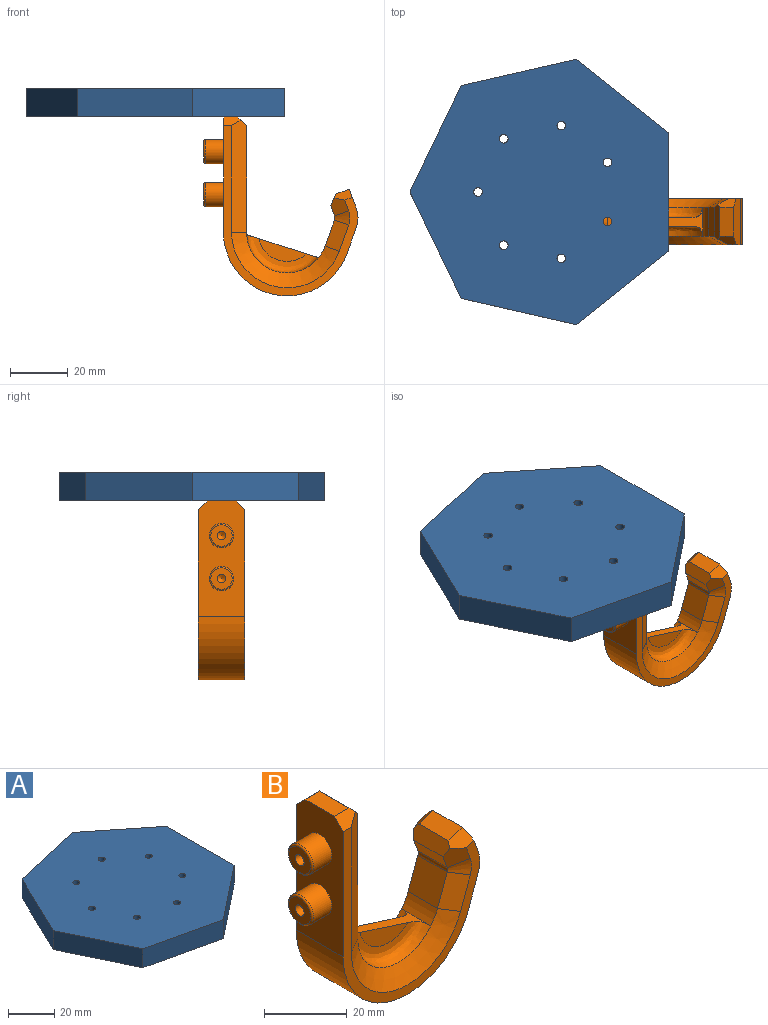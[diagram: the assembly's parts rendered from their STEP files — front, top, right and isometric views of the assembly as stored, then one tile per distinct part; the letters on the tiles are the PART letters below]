
ASSEMBLY  parts=2 mates=1
PART A: 16 faces, bbox 89.7x92x10 mm
  f0: plane 40.93x10mm, normal (1,0,0), area 409.3mm2, adj f1,f6,f7,f8
  f1: plane 32x25.52mm, normal (0.62,0.78,0), area 409.3mm2, adj f0,f2,f7,f8
  f2: plane 39.91x10mm, normal (-0.22,0.97,0), area 409.3mm2, adj f1,f3,f7,f8
  f3: plane 36.88x17.76mm, normal (-0.9,0.43,0), area 409.3mm2, adj f2,f4,f7,f8
  f4: plane 36.88x17.76mm, normal (-0.9,-0.43,0), area 409.3mm2, adj f3,f5,f7,f8
  f5: plane 39.91x10mm, normal (-0.22,-0.97,0), area 409.3mm2, adj f4,f6,f7,f8
  f6: plane 32x25.52mm, normal (0.62,-0.78,0), area 409.3mm2, adj f0,f5,f7,f8
  f7: plane 91.98x89.67mm, normal (0,0,1), area 6039.4mm2, adj f0,f1,f2,f3,f4,f5,f6,f9
  f8: plane 91.98x89.67mm, normal (0,0,-1), area 6039.4mm2, adj f0,f1,f2,f3,f4,f5,f6,f9
  f9: cylinder r=1.5mm len=10mm, axis (0,0,-1), area 94.2mm2, adj f7,f8
  f10: cylinder r=1.5mm len=10mm, axis (0,0,-1), area 94.2mm2, adj f7,f8
  f11: cylinder r=1.5mm len=10mm, axis (0,0,-1), area 94.2mm2, adj f7,f8
  f12: cylinder r=1.5mm len=10mm, axis (0,0,-1), area 94.2mm2, adj f7,f8
  f13: cylinder r=1.5mm len=10mm, axis (0,0,-1), area 94.2mm2, adj f7,f8
  f14: cylinder r=1.5mm len=10mm, axis (0,0,-1), area 94.2mm2, adj f7,f8
  f15: cylinder r=1.5mm len=10mm, axis (0,0,-1), area 94.2mm2, adj f7,f8
PART B: 46 faces, bbox 54.6x17.2x63.2 mm
  f0: cylinder r=14mm len=10mm, axis (0,-1,0), area 45.7mm2, adj f10,f12,f13,f35
  f1: plane 10x5mm, normal (0,0,1), area 50mm2, adj f6,f41,f42,f43
  f2: plane 10x4.7mm, normal (-0.34,0,0.94), area 50mm2, adj f23,f38,f39,f40
  f3: plane 37x10mm, normal (1,0,0), area 370mm2, adj f4,f8,f9,f43
  f4: plane 38.9x5.2mm, normal (0.5,-0.87,0), area 227.8mm2, adj f3,f5,f10,f42,f43
  f5: plane 59x46.59mm, normal (0,-1,0), area 319.8mm2, adj f4,f6,f10,f11,f14,f15,f18,f19
  f6: plane 40x16mm, normal (-1,0,0), area 520.2mm2, adj f1,f5,f7,f11,f25,f27,f41,f42
  f7: plane 59x46.59mm, normal (0,1,0), area 319.8mm2, adj f6,f8,f11,f12,f15,f16,f19,f20
  f8: plane 38.9x5.2mm, normal (0.5,0.87,0), area 227.8mm2, adj f3,f7,f12,f41,f43
  f9: cylinder r=14mm len=10mm, axis (0,-1,0), area 8.4mm2, adj f3,f10,f12,f35
  f10: cone r=14mm half-angle=60deg, axis (0,-1,0), area 278.3mm2, adj f0,f4,f5,f9,f14,f36
  f11: cylinder r=22mm len=42.67mm, axis (0,-1,0), area 983mm2, adj f5,f6,f7,f15
  f12: cone r=19.2mm half-angle=60deg, axis (0,1,0), area 278.3mm2, adj f0,f7,f8,f9,f16,f37
  f13: plane 10x9.1mm, normal (-0.94,0,0.34), area 96.9mm2, adj f0,f14,f16,f17
  f14: plane 10.88x8.2mm, normal (-0.47,-0.87,0.17), area 58.2mm2, adj f5,f10,f13,f18
  f15: plane 16x9.1mm, normal (0.94,0,-0.34), area 155mm2, adj f5,f7,f11,f19
  f16: plane 10.88x8.2mm, normal (-0.47,0.87,0.17), area 58.2mm2, adj f7,f12,f13,f20
  f17: cylinder r=2mm len=10mm, axis (0,-1,0), area 14mm2, adj f13,f18,f20,f21
  f18: cone r=2mm half-angle=60deg, axis (0,-1,0), area 19.3mm2, adj f5,f14,f17,f22
  f19: cylinder r=10mm len=16mm, axis (0,-1,0), area 111.7mm2, adj f5,f7,f15,f23
  f20: cone r=7.2mm half-angle=60deg, axis (0,1,0), area 19.3mm2, adj f7,f16,f17,f24
  f21: plane 10x3.76mm, normal (-0.94,0,-0.34), area 40mm2, adj f17,f22,f24,f40
  f22: plane 6.26x6.2mm, normal (-0.47,-0.87,-0.17), area 29.7mm2, adj f5,f18,f21,f39,f40
  f23: plane 16x6.58mm, normal (0.94,0,0.34), area 103mm2, adj f2,f5,f7,f19,f38,f39
  f24: plane 6.26x6.2mm, normal (-0.47,0.87,-0.17), area 29.7mm2, adj f7,f20,f21,f38,f40
  f25: cylinder r=4.2mm len=8.4mm, axis (1,0,0), area 166.3mm2, adj f6,f45
  f26: plane 7.4x7.4mm, normal (-1,0,0), area 35.9mm2, adj f30,f45
  f27: cylinder r=4.2mm len=8.4mm, axis (1,0,0), area 166.3mm2, adj f6,f44
  f28: plane 7.4x7.4mm, normal (-1,0,0), area 35.9mm2, adj f32,f44
  f29: cone r=0mm half-angle=59deg, axis (-1,0,0), area 8.2mm2, adj f30
  f30: cylinder r=1.5mm len=12mm, axis (-1,0,0), area 113.1mm2, adj f26,f29
  f31: cone r=0mm half-angle=59deg, axis (-1,0,0), area 8.2mm2, adj f32
  f32: cylinder r=1.5mm len=12mm, axis (-1,0,0), area 113.1mm2, adj f28,f31
  f33: plane 16.55x7.9mm, normal (0,-1,0), area 61.6mm2, adj f35,f36
  f34: plane 16.55x7.9mm, normal (0,1,0), area 61.6mm2, adj f35,f37
  f35: plane 26.09x11.19mm, normal (0.3,0,0.95), area 88.5mm2, adj f0,f9,f33,f34,f36,f37
  f36: bspline ~24.9x13.4mm, area 173.7mm2, adj f10,f33,f35
  f37: bspline ~24.9x13.4mm, area 173.7mm2, adj f12,f34,f35
  f38: plane 6.38x3.78mm, normal (-0.24,0.71,0.66), area 20.6mm2, adj f2,f7,f23,f24,f40
  f39: plane 6.38x3.78mm, normal (-0.24,-0.71,0.66), area 20.6mm2, adj f2,f5,f22,f23,f40
  f40: plane 12.2x3.85mm, normal (-0.91,0,0.42), area 47.1mm2, adj f2,f21,f22,f24,f38,f39
  f41: plane 6.1x3mm, normal (0,0.71,0.71), area 20.6mm2, adj f1,f6,f7,f8,f43
  f42: plane 6.1x3mm, normal (0,-0.71,0.71), area 20.6mm2, adj f1,f4,f5,f6,f43
  f43: plane 12.2x3mm, normal (0.71,0,0.71), area 47.1mm2, adj f1,f3,f4,f8,f41,f42
  f44: torus R=3.7mm, axis (-1,0,0), area 19.8mm2, adj f27,f28
  f45: torus R=3.7mm, axis (-1,0,0), area 19.8mm2, adj f25,f26
PLACE A at identity fixed
PLACE B t=(21.25,-10.23,0)mm
MATE fastened B.f1 <-> A.f11  axis (0,0,1) through (21.25,-10.23,0)mm
